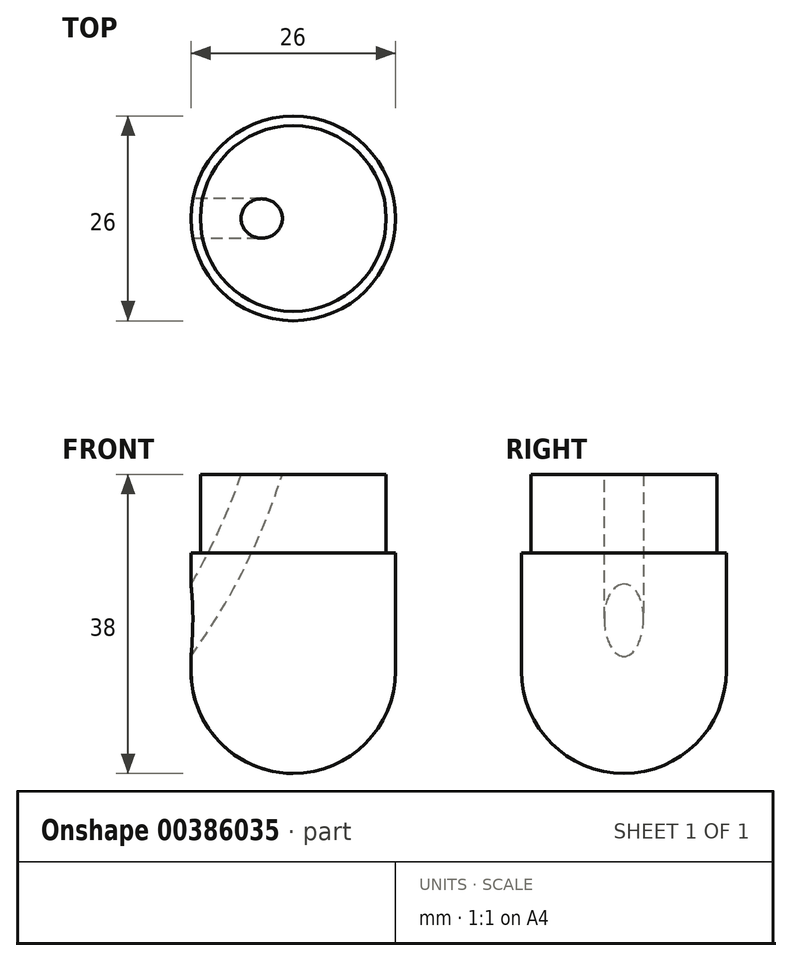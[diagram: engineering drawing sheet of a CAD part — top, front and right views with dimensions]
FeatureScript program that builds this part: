
annotation { "Feature Type Name" : "Feature", "Feature Type Description" : "" }
export const myFeature = defineFeature(function(context is Context, id is Id, definition is map)
    precondition{}
    {
        {
            var Q0;
            Q0=qCreatedBy(makeId("Top.planeOp"),FACE);
            var sketch = newSketch(context, id + "F0", { "sketchPlane" : qUnion([Q0])});
            skCircle(sketch, "E0", {"center": v(0, 0) * mm, "radius": 13 * mm});
            skSolve(sketch);
        }
        {
            var Q0;
            Q0=makeQuery(id+"F0.imprint","IMPRINT",FACE,{"disambiguationData":[TD([[makeQuery(id+"F0.imprint","IMPRINT",EDGE,{"derivedFrom":sQuery(id+"F0.wireOp",EDGE,"E0")}),1.0]])]});
            extrude(context, id + "F1", {"entities" : qUnion([Q0]), "depth" : 25 * mm});
        }
        {
            var Q0;
            Q0=makeQuery(id+"F1.opExtrude","CAP_FACE",FACE,{"disambiguationData":[OSD([sQuery(id+"F0.wireOp",EDGE,"E0")])],"isStart":false});
            var sketch = newSketch(context, id + "F2", { "sketchPlane" : qUnion([Q0])});
            skCircle(sketch, "E1", {"center": v(0, 0) * mm, "radius": 3 * mm});
            skCircle(sketch, "E2", {"center": v(0, 0) * mm, "radius": 11.8 * mm});
            skSolve(sketch);
        }
        {
            var Q0;
            Q0=qCreatedBy(makeId("Front.planeOp"),FACE);
            var sketch = newSketch(context, id + "F3", { "sketchPlane" : qUnion([Q0])});
            skCircle(sketch, "E3", {"center": v(-50, 50) * mm, "radius": 2.5 * mm});
            skPoint(sketch, "E4", {"position": v(-80, 50) * mm});
            skLineSegment(sketch, "E5", {"start": v(-58.85, 50) * mm, "end": v(-118.37, 50) * mm});
            skSolve(sketch);
        }
        {
            var Q0;
            Q0=qCreatedBy(makeId("Top.planeOp"),FACE);
            var sketch = newSketch(context, id + "F4", { "sketchPlane" : qUnion([Q0])});
            skPoint(sketch, "E6", {"position": v(-50, 0) * mm});
            skPoint(sketch, "E7", {"position": v(-130, 0) * mm});
            skCircle(sketch, "E8", {"center": v(-130, 0) * mm, "radius": 80 * mm});
            skSolve(sketch);
        }
        {
            var Q0;
            Q0=makeQuery(id+"F3.imprint","IMPRINT",FACE,{"disambiguationData":[TD([[makeQuery(id+"F3.imprint","IMPRINT",EDGE,{"derivedFrom":sQuery(id+"F3.wireOp",EDGE,"E3")}),1.0]])]});
            var Q1;
            Q1=sQuery(id+"F4.wireOp",EDGE,"E8");
            revolve(context, id + "F5", {"entities" : qUnion([Q0]), "axis" : qUnion([Q1]), "revolveType" : RevolveType.FULL});
        }
        {
            var Q0;
            Q0=makeQuery(id+"F5.opRevolve","SWEPT_BODY",BODY,{"disambiguationData":[OSD([sQuery(id+"F3.wireOp",EDGE,"E3")])]});
            transform(context, id + "F6", {"entities" : qUnion([Q0]), "transformType" : TransformType.TRANSLATION_3D, "dx" : 50 * mm, "dy" : 0 * mm, "dz" : 0 * mm, "makeCopy" : false});
        }
        {
            var Q0;
            Q0=makeQuery(id+"F5.opRevolve","SWEPT_BODY",BODY,{"disambiguationData":[OSD([sQuery(id+"F3.wireOp",EDGE,"E3")])]});
            var Q1;
            Q1=sQuery(id+"F3.wireOp",EDGE,"E5");
            transform(context, id + "F7", {"entities" : qUnion([Q0]), "transformType" : TransformType.ROTATION, "transformAxis" : qUnion([Q1]), "angle" : 90 * degree, "makeCopy" : false});
        }
        {
            var Q0;
            Q0=qCreatedBy(makeId("Front.planeOp"),FACE);
            var sketch = newSketch(context, id + "F8", { "sketchPlane" : qUnion([Q0])});
            skArc(sketch, "E9", {"start": v(0, -13) * mm, "mid": v(9.2, -9.2) * mm, "end": v(13, 0) * mm});
            skLineSegment(sketch, "E10", {"start": v(0, 0) * mm, "end": v(13, 0) * mm});
            skLineSegment(sketch, "E11", {"start": v(0, 0) * mm, "end": v(0, -13) * mm});
            skSolve(sketch);
        }
        {
            var Q0;
            Q0 = qSketchRegion(id + "F8", true);
            var Q1;
            Q1=makeQuery(id+"F1.opExtrude","CAP_EDGE",EDGE,{"disambiguationData":[OSD([sQuery(id+"F0.wireOp",EDGE,"E0")])],"isStart":true});
            revolve(context, id + "F9", {"operationType" : NewBodyOperationType.ADD, "entities" : qUnion([Q0]), "axis" : qUnion([Q1]), "revolveType" : RevolveType.FULL});
        }
        {
            var Q0;
            Q0=makeQuery(id+"F2.imprint","IMPRINT",FACE,{"disambiguationData":[TD([[makeQuery(id+"F2.imprint","IMPRINT",EDGE,{"derivedFrom":sQuery(id+"F2.wireOp",EDGE,"E2")}),-1.0]])]});
            extrude(context, id + "F10", {"entities" : qUnion([Q0]), "operationType" : NewBodyOperationType.REMOVE, "oppositeDirection" : true, "depth" : 10 * mm});
        }
        {
            var Q0;
            Q0=makeQuery(id+"F5.opRevolve","SWEPT_BODY",BODY,{"disambiguationData":[OSD([sQuery(id+"F3.wireOp",EDGE,"E3")])]});
            var Q1;
            Q1=makeQuery(id+"F1.opExtrude","SWEPT_BODY",BODY,{"disambiguationData":[OSD([sQuery(id+"F0.wireOp",EDGE,"E0")])]});
            booleanBodies(context, id + "F11", {"operationType" : BooleanOperationType.SUBTRACTION, "tools" : qUnion([Q0]), "targets" : qUnion([Q1])});
        }
    });
